# Revit family: Pottorff_EDV-545-MD_R20
name_source: partatom
category: Mechanical Equipment
units: mm (PartAtom-declared; Revit-internal decimal feet)

## family parameters
Cut with Voids When Loaded = No
Host = Face
Part Type = Normal
Room Calculation Point = No
Round Connector Dimension = Use Diameter
Shared = No

## types (2) — shared parameters
Air Volume Delivered = 10,038 cfm
Assembly Code = B3020300
Blades (Front) = 45° x .08'' thick horizontal J style.
Blades (Rear) = 45° x .05'' thick vertical chevron style.
Default Elevation = 0"
Depth = 5 3/8"
Description = The EDV-545-MD dual-module louver is engineered and tested to withstand extreme loads, debris impact, and cyclic fatigue associated with the severe weather effects of hurricanes (Miami-Dade County approval NOA No. 22-0118.04) while maintaining maximum water infiltration resistance at a minimum louver depth. The front (exterior) side of the louver features horizontal J-style blades for a pleasant architectural appearance. The (interior) side features vertical chevron blades which provide superior resistance to wind-driven rain. For installation, the EDV-545-MD offers a continuous angle. The EDV-545-MD is AMCA 540 and 550 listed, making it ideally suited for use in hurricane-prone and wind-borne debris regions as per the International Building Code.
Design Load = 100 psf
Frame = 5-3/8'' deep x 0.081'' thick channel.
Free Area (48" x 48") = 8.03 ft² 50.2%
Free Area Velocity = 1250 fpm
Manufacturer = Pottorff
Material = Mill finish 6005A-T5 extruded aluminum.
Maximum Height = 96"
Maximum Width = 60"
Minimum Height = 12"
Minimum Width = 12"
Model = EDV-545-MD
Modeled By = Commense Studio
Mullion = Visible
Offset_Bottom = 1"
Offset_Top = 2 3/8"
Offset_Vertical = 1"
Pressure Loss = .55 in. wg
Screen = 1/2'' x 0.063'' expanded and flattened aluminum.
URL = https://www.pottorff.com
Velocity @ .15 in.wg. Pressure Loss = 666 fpm

## per-type parameters (varying)
| type | Array Control 2 | Array Control_H | Array Control_V | Blade Height | Blade Width | Height | Height Control | Width | Width Control |
| 60" x 96" | 47 | 47 | 66 | 94" | 58" | 120" | 96" | 60" | 60" |
| 30" x 48" | 22 | 22 | 39 | 46" | 34" | 48" | 48" | 36" | 36" |

## geometry (parser evidence)
native form markers: Blend x4, Sweep x11
no freeform markers — native parametric forms only
